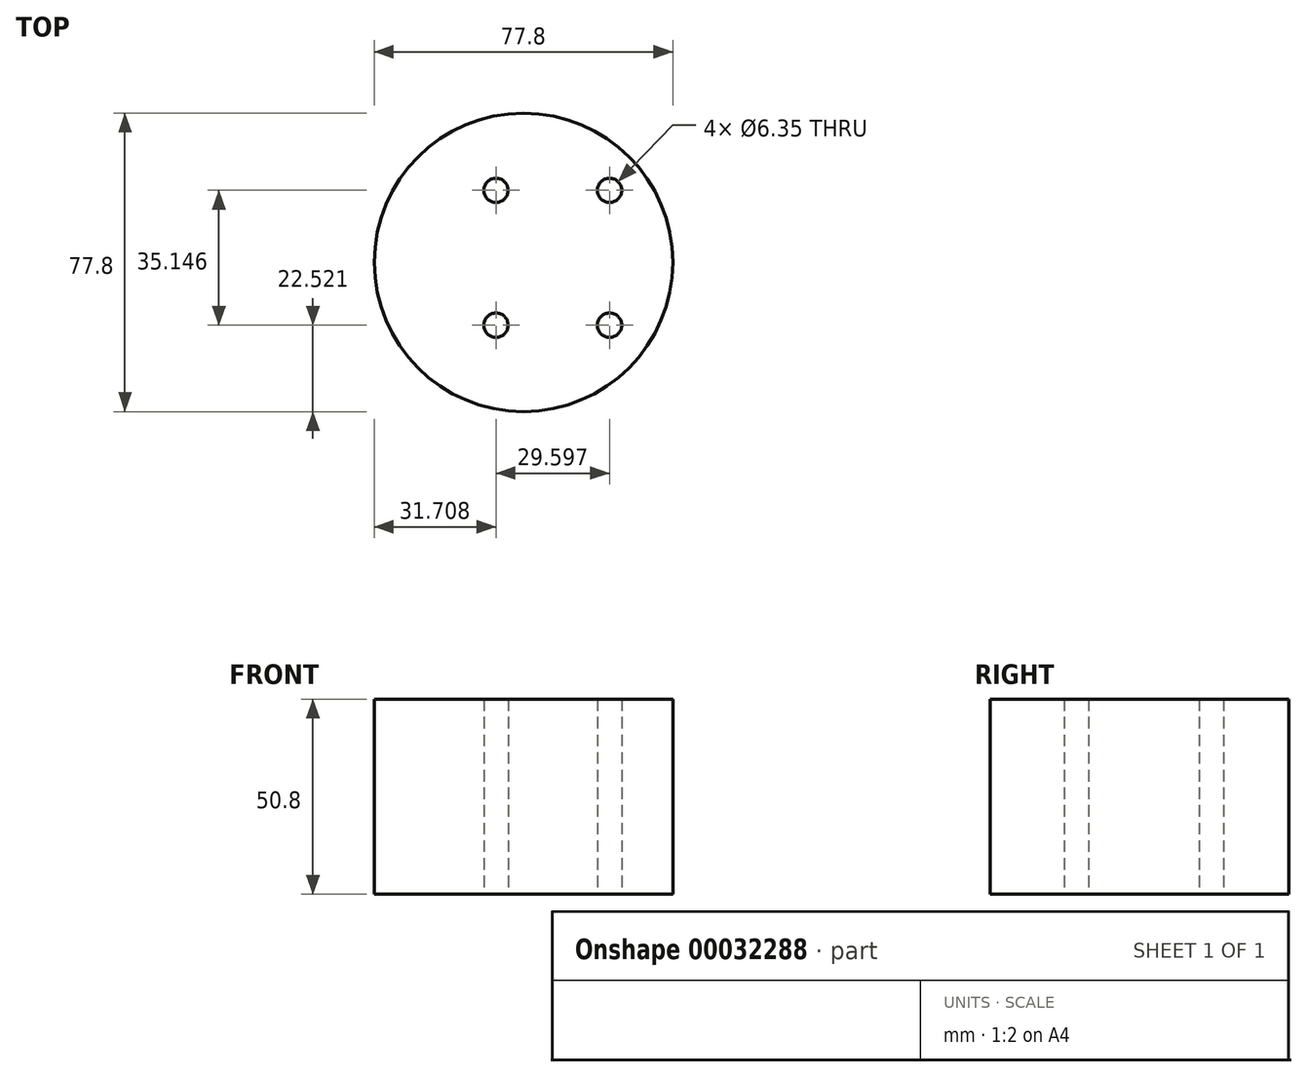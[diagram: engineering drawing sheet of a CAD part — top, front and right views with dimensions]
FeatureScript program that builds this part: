
annotation { "Feature Type Name" : "Feature", "Feature Type Description" : "" }
export const myFeature = defineFeature(function(context is Context, id is Id, definition is map)
    precondition{}
    {
        {
            var Q0;
            Q0=qCreatedBy(makeId("Top.planeOp"),FACE);
            var sketch = newSketch(context, id + "F0", { "sketchPlane" : qUnion([Q0])});
            skCircle(sketch, "E0", {"center": v(0, 0) * mm, "radius": 38.9 * mm});
            skSolve(sketch);
        }
        {
            var Q0;
            Q0 = qSketchRegion(id + "F0", true);
            extrude(context, id + "F1", {"entities" : qUnion([Q0]), "depth" : 25.4 * mm, "hasSecondDirection" : true, "secondDirectionOppositeDirection" : true, "secondDirectionDepth" : 25.4 * mm});
        }
        {
            var Q0;
            Q0=makeQuery(id+"F1.opExtrude","CAP_FACE",FACE,{"disambiguationData":[OSD([sQuery(id+"F0.wireOp",EDGE,"E0")])],"isStart":true});
            var sketch = newSketch(context, id + "F2", { "sketchPlane" : qUnion([Q0])});
            skLineSegment(sketch, "E1.bottom", {"start": v(-7.2, -18.77) * mm, "end": v(22.4, -18.77) * mm});
            skLineSegment(sketch, "E1.top", {"start": v(-7.2, 16.38) * mm, "end": v(22.4, 16.38) * mm});
            skLineSegment(sketch, "E1.left", {"start": v(-7.2, -18.77) * mm, "end": v(-7.2, 16.38) * mm});
            skLineSegment(sketch, "E1.right", {"start": v(22.4, -18.77) * mm, "end": v(22.4, 16.38) * mm});
            skSolve(sketch);
        }
        {
            var Q0;
            Q0=sQuery(id+"F2.wireOp",VERTEX,"E1.top.end");
            var Q1;
            Q1=sQuery(id+"F2.wireOp",VERTEX,"E1.left.start");
            var Q2;
            Q2=sQuery(id+"F2.wireOp",VERTEX,"E1.left.end");
            var Q3;
            Q3=sQuery(id+"F2.wireOp",VERTEX,"E1.right.start");
            var Q4;
            Q4=sQuery(id+"F2.wireOp",VERTEX,"E1.right.end");
            var Q5;
            Q5=sQuery(id+"F2.wireOp",VERTEX,"E1.bottom.start");
            var Q6;
            Q6=sQuery(id+"F2.wireOp",VERTEX,"E1.bottom.end");
            var Q7;
            Q7=sQuery(id+"F2.wireOp",VERTEX,"E1.top.start");
            var Q8;
            Q8=makeQuery(id+"F1.opExtrude","SWEPT_BODY",BODY,{"disambiguationData":[OSD([sQuery(id+"F0.wireOp",EDGE,"E0")])]});
            hole(context, id + "F3", {"style" : HoleStyle.SIMPLE, "holeDiameter" : 6.35 * mm, "endStyle" : HoleEndStyle.THROUGH, "locations" : qUnion([Q0, Q1, Q2, Q3, Q4, Q5, Q6, Q7]), "scope" : qUnion([Q8])});
        }
    });
